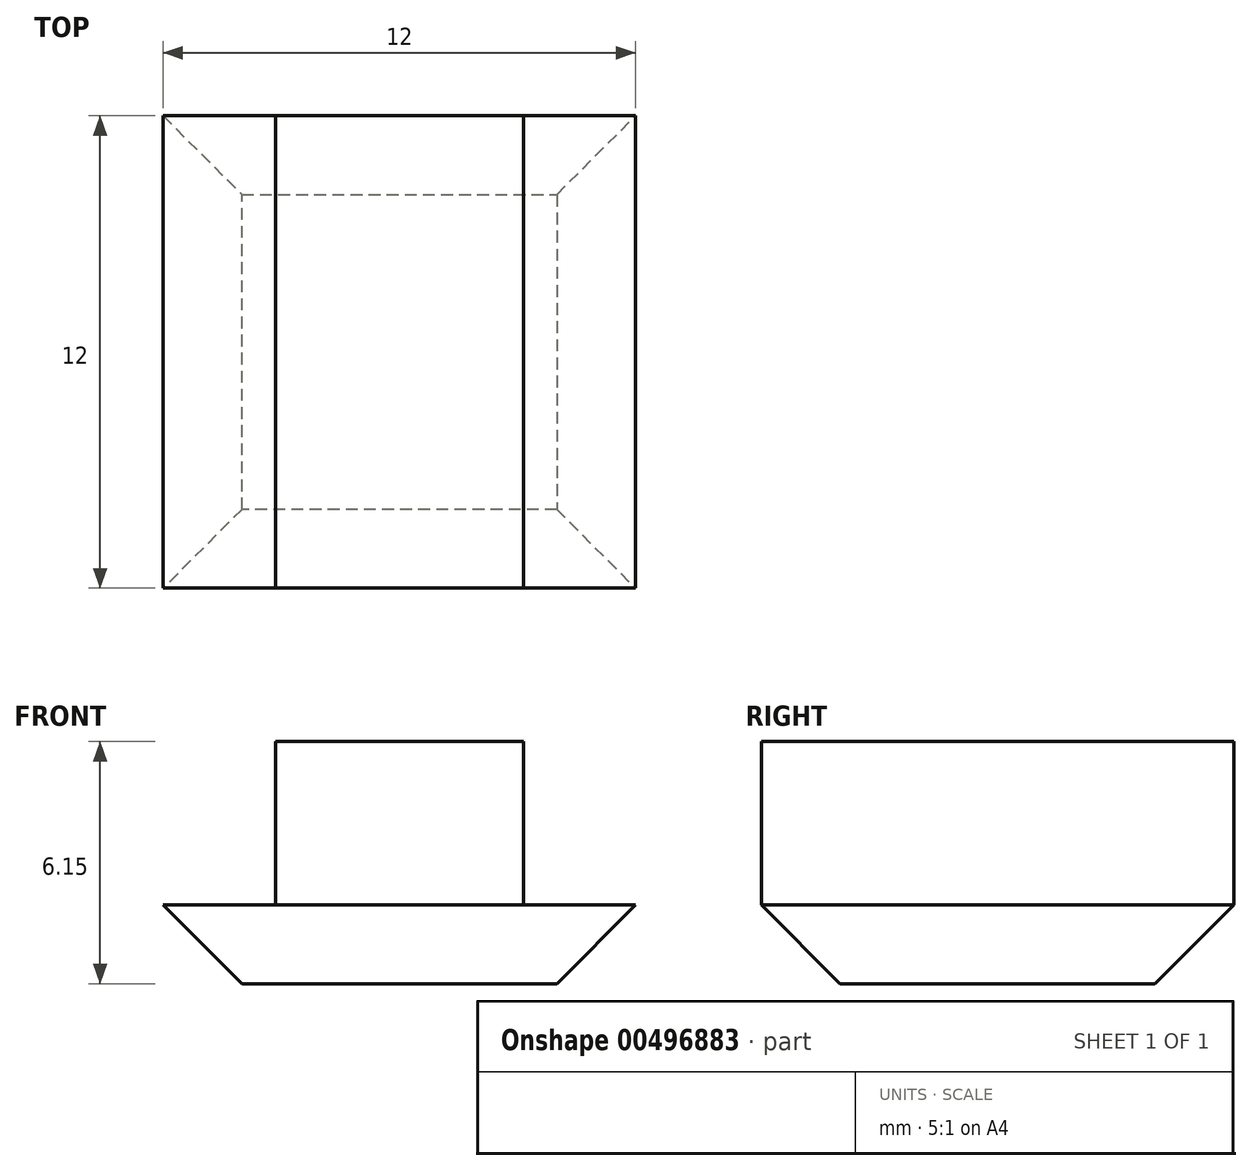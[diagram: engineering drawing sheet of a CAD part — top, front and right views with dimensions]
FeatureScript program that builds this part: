
annotation { "Feature Type Name" : "Feature", "Feature Type Description" : "" }
export const myFeature = defineFeature(function(context is Context, id is Id, definition is map)
    precondition{}
    {
        {
            var Q0;
            Q0=qCreatedBy(makeId("Top.planeOp"),FACE);
            var sketch = newSketch(context, id + "F0", { "sketchPlane" : qUnion([Q0])});
            skLineSegment(sketch, "E0.bottom", {"start": v(-6, 6) * mm, "end": v(6, 6) * mm});
            skLineSegment(sketch, "E0.top", {"start": v(-6, -6) * mm, "end": v(6, -6) * mm});
            skLineSegment(sketch, "E0.left", {"start": v(-6, 6) * mm, "end": v(-6, -6) * mm});
            skLineSegment(sketch, "E0.right", {"start": v(6, 6) * mm, "end": v(6, -6) * mm});
            skSolve(sketch);
        }
        {
            var Q0;
            Q0 = qSketchRegion(id + "F0", true);
            extrude(context, id + "F1", {"entities" : qUnion([Q0]), "depth" : 2 * mm});
        }
        {
            var Q0;
            Q0=makeQuery(id+"F1.opExtrude","CAP_FACE",FACE,{"disambiguationData":[OSD([sQuery(id+"F0.wireOp",EDGE,"E0.bottom"),sQuery(id+"F0.wireOp",EDGE,"E0.top"),sQuery(id+"F0.wireOp",EDGE,"E0.left"),sQuery(id+"F0.wireOp",EDGE,"E0.right")])],"isStart":false});
            var sketch = newSketch(context, id + "F2", { "sketchPlane" : qUnion([Q0])});
            skLineSegment(sketch, "E1", {"start": v(-3.15, 6) * mm, "end": v(-3.15, -6) * mm});
            skLineSegment(sketch, "E2", {"start": v(3.15, 6) * mm, "end": v(3.15, -6) * mm});
            skSolve(sketch);
        }
        {
            var Q0;
            Q0 = qSketchRegion(id + "F2", true);
            var Q1;
            {var subQ0=sQuery(id+"F2.wireOp",EDGE,"E1");Q1=makeQuery(id+"F2.imprint","IMPRINT",FACE,{"disambiguationData":[TD([[makeQuery(id+"F2.imprint","IMPRINT",EDGE,{"derivedFrom":subQ0}),1.0]])]});}
            extrude(context, id + "F3", {"entities" : qUnion([Q0, Q1]), "operationType" : NewBodyOperationType.ADD, "depth" : 4.15 * mm});
        }
        {
            var Q0;
            Q0=makeQuery(id+"F1.opExtrude","CAP_EDGE",EDGE,{"disambiguationData":[OSD([sQuery(id+"F0.wireOp",EDGE,"E0.right")])],"isStart":true});
            var Q1;
            Q1=makeQuery(id+"F1.opExtrude","CAP_EDGE",EDGE,{"disambiguationData":[OSD([sQuery(id+"F0.wireOp",EDGE,"E0.top")])],"isStart":true});
            var Q2;
            Q2=makeQuery(id+"F1.opExtrude","CAP_EDGE",EDGE,{"disambiguationData":[OSD([sQuery(id+"F0.wireOp",EDGE,"E0.left")])],"isStart":true});
            var Q3;
            Q3=makeQuery(id+"F1.opExtrude","CAP_EDGE",EDGE,{"disambiguationData":[OSD([sQuery(id+"F0.wireOp",EDGE,"E0.bottom")])],"isStart":true});
            chamfer(context, id + "F4", {"entities" : qUnion([Q0, Q1, Q2, Q3]), "width" : 2 * mm, "tangentPropagation" : true});
        }
    });
